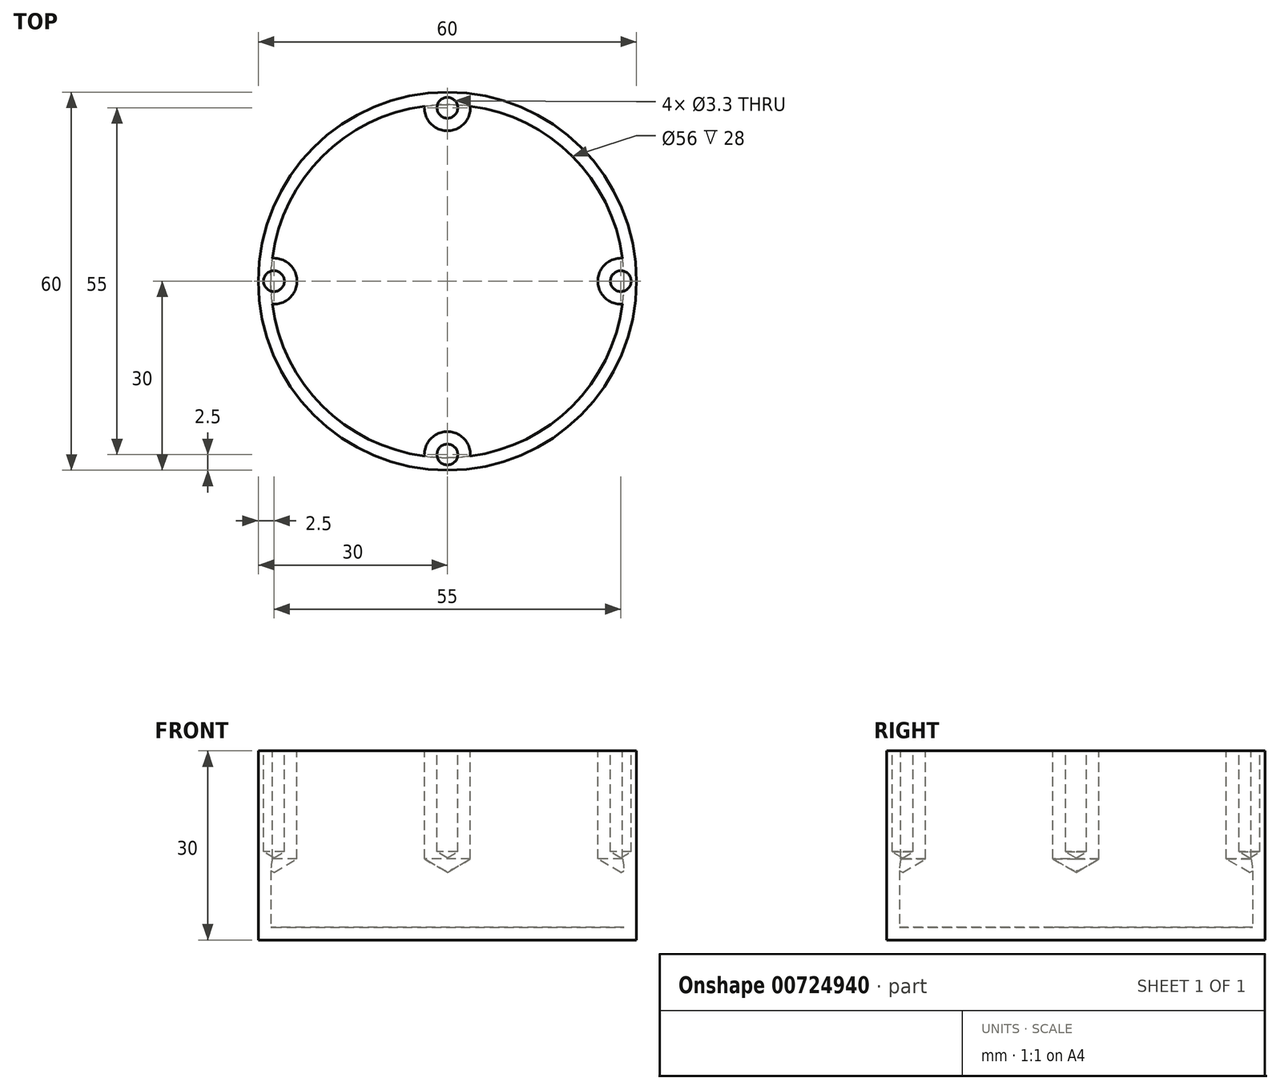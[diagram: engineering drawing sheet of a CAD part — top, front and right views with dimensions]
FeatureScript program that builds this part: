
annotation { "Feature Type Name" : "Feature", "Feature Type Description" : "" }
export const myFeature = defineFeature(function(context is Context, id is Id, definition is map)
    precondition{}
    {
        {
            var Q0;
            Q0=qCreatedBy(makeId("Top.planeOp"),FACE);
            var sketch = newSketch(context, id + "F0", { "sketchPlane" : qUnion([Q0])});
            skCircle(sketch, "E0", {"center": v(0, 0) * mm, "radius": 30 * mm});
            skSolve(sketch);
        }
        {
            var Q0;
            Q0=makeQuery(id+"F0.imprint","IMPRINT",FACE,{"disambiguationData":[TD([[makeQuery(id+"F0.imprint","IMPRINT",EDGE,{"derivedFrom":sQuery(id+"F0.wireOp",EDGE,"E0")}),1.0]])]});
            extrude(context, id + "F1", {"entities" : qUnion([Q0]), "depth" : 30 * mm, "offsetDistance" : 25 * mm});
        }
        {
            var Q0;
            Q0=makeQuery(id+"F1.opExtrude","CAP_FACE",FACE,{"disambiguationData":[OSD([sQuery(id+"F0.wireOp",EDGE,"E0")])],"isStart":false});
            var sketch = newSketch(context, id + "F2", { "sketchPlane" : qUnion([Q0])});
            skCircle(sketch, "E1", {"center": v(0, 0) * mm, "radius": 27.5 * mm});
            skPoint(sketch, "E2", {"position": v(0, 27.5) * mm});
            skPoint(sketch, "E3", {"position": v(27.5, 0) * mm});
            skPoint(sketch, "E4", {"position": v(0, -27.5) * mm});
            skPoint(sketch, "E5", {"position": v(-27.5, 0) * mm});
            skCircle(sketch, "E6", {"center": v(0, 27.5) * mm, "radius": 1.5 * mm});
            skCircle(sketch, "E7.1.0", {"center": v(-27.5, 0) * mm, "radius": 1.5 * mm});
            skCircle(sketch, "E7.2.0", {"center": v(0, -27.5) * mm, "radius": 1.5 * mm});
            skCircle(sketch, "E7.3.0", {"center": v(27.5, 0) * mm, "radius": 1.5 * mm});
            skSolve(sketch);
        }
        {
            var Q0;
            Q0=sQuery(id+"F2.wireOp",VERTEX,"E2");
            var Q1;
            Q1=sQuery(id+"F2.wireOp",VERTEX,"E5");
            var Q2;
            Q2=sQuery(id+"F2.wireOp",VERTEX,"E4");
            var Q3;
            Q3=sQuery(id+"F2.wireOp",VERTEX,"E3");
            var Q4;
            Q4=makeQuery(id+"F1.opExtrude","SWEPT_BODY",BODY,{"disambiguationData":[OSD([sQuery(id+"F0.wireOp",EDGE,"E0")])]});
            hole(context, id + "F3", {"style" : HoleStyle.SIMPLE, "endStyle" : HoleEndStyle.BLIND, "standardTappedOrClearance" : lookupTablePath({ "standard" : "ISO", "fit" : "Normal", "size" : "M3", "type" : "Clearance" }), "standardBlindInLast" : lookupTablePath({ "fit" : "Standard", "standard" : "ISO", "size" : "M3", "type" : "Clearance" }), "holeDiameter" : 3.3 * mm, "majorDiameter" : 5 * mm, "holeDepth" : 16 * mm, "isTappedThrough" : true, "tappedDepth" : 12 * mm, "tapClearance" : 3, "locations" : qUnion([Q0, Q1, Q2, Q3]), "scope" : qUnion([Q4])});
        }
        {
            var Q0;
            Q0=makeQuery(id+"F1.opExtrude","CAP_FACE",FACE,{"disambiguationData":[OSD([sQuery(id+"F0.wireOp",EDGE,"E0")])],"isStart":false});
            shell(context, id + "F4", {"entities" : qUnion([Q0]), "thickness" : 2 * mm});
        }
    });
